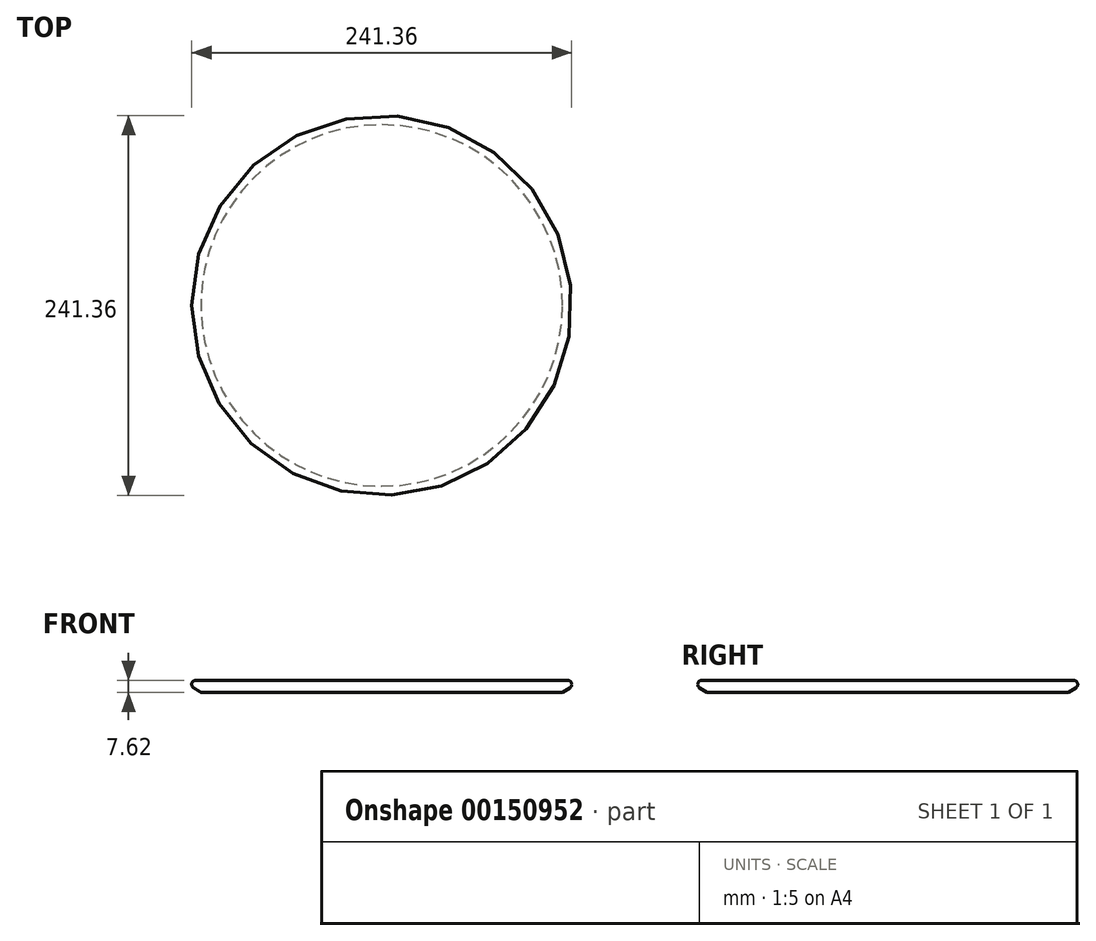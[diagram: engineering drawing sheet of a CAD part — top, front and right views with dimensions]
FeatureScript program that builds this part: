
annotation { "Feature Type Name" : "Feature", "Feature Type Description" : "" }
export const myFeature = defineFeature(function(context is Context, id is Id, definition is map)
    precondition{}
    {
        {
            var Q0;
            Q0=qCreatedBy(makeId("Front.planeOp"),FACE);
            var sketch = newSketch(context, id + "F0", { "sketchPlane" : qUnion([Q0])});
            skLineSegment(sketch, "E0", {"start": v(0, 0) * mm, "end": v(127, 0) * mm});
            skLineSegment(sketch, "E1", {"start": v(127, 0) * mm, "end": v(114.8, -7.62) * mm});
            skLineSegment(sketch, "E2", {"start": v(114.8, -7.62) * mm, "end": v(0, -7.62) * mm});
            skLineSegment(sketch, "E3", {"start": v(0, -7.62) * mm, "end": v(0, 0) * mm});
            skSolve(sketch);
        }
        {
            var Q0;
            Q0=makeQuery(id+"F0.imprint","IMPRINT",FACE,{"disambiguationData":[TD([[makeQuery(id+"F0.imprint","IMPRINT",EDGE,{"derivedFrom":sQuery(id+"F0.wireOp",EDGE,"E0")}),-1.0]])]});
            var Q1;
            Q1=sQuery(id+"F0.wireOp",EDGE,"E3");
            revolve(context, id + "F1", {"entities" : qUnion([Q0]), "axis" : qUnion([Q1]), "revolveType" : RevolveType.FULL});
        }
        {
            var Q0;
            Q0=makeQuery(id+"F1.opRevolve","SWEPT_FACE",FACE,{"disambiguationData":[OSD([sQuery(id+"F0.wireOp",EDGE,"E0")])]});
            fillet(context, id + "F2", {"entities" : qUnion([Q0]), "radius" : 2.54 * mm, "tangentPropagation" : true, "allowEdgeOverflow" : false});
        }
    });
